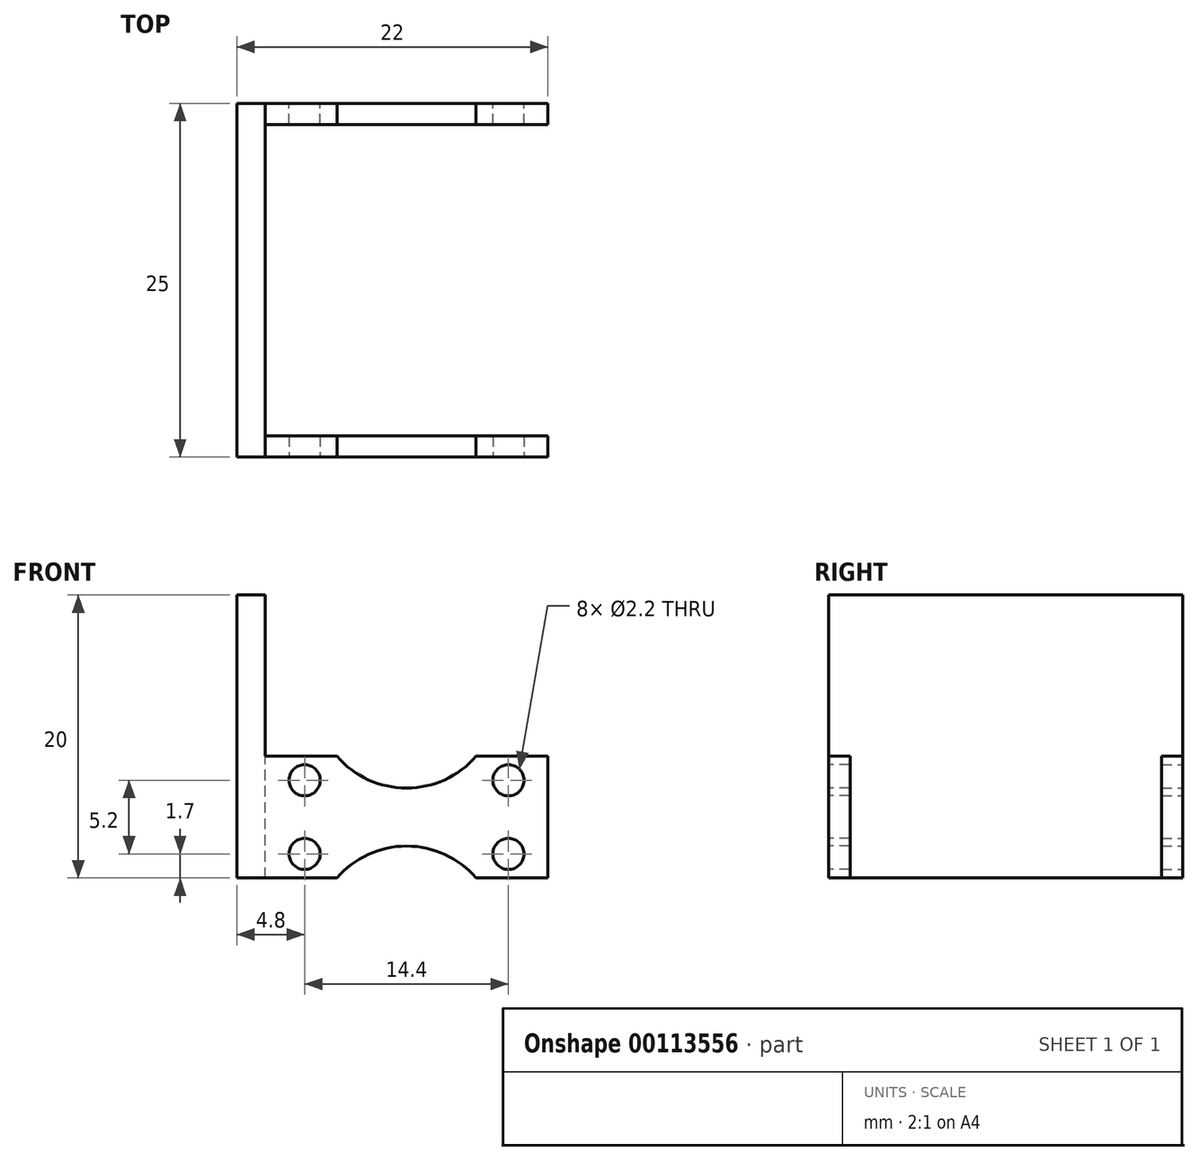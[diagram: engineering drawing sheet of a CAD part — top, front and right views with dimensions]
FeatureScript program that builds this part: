
annotation { "Feature Type Name" : "Feature", "Feature Type Description" : "" }
export const myFeature = defineFeature(function(context is Context, id is Id, definition is map)
    precondition{}
    {
        {
            var Q0;
            Q0=qCreatedBy(makeId("Front.planeOp"),FACE);
            var sketch = newSketch(context, id + "F0", { "sketchPlane" : qUnion([Q0])});
            skLineSegment(sketch, "E0.bottom", {"start": v(0, 0) * mm, "end": v(20, 0) * mm});
            skLineSegment(sketch, "E0.top", {"start": v(0, 8.6) * mm, "end": v(20, 8.6) * mm});
            skLineSegment(sketch, "E0.left", {"start": v(0, 0) * mm, "end": v(0, 8.6) * mm});
            skLineSegment(sketch, "E0.right", {"start": v(20, 0) * mm, "end": v(20, 8.6) * mm});
            skSolve(sketch);
        }
        {
            var Q0;
            Q0=qSketchRegion(id+"F0",true);
            extrude(context, id + "F1", {"entities" : qUnion([Q0]), "depth" : 1.5 * mm});
        }
        {
            var Q0;
            Q0=makeQuery(id+"F1.opExtrude","CAP_FACE",FACE,{"disambiguationData":[OSD([sQuery(id+"F0.wireOp",EDGE,"E0.bottom"),sQuery(id+"F0.wireOp",EDGE,"E0.top"),sQuery(id+"F0.wireOp",EDGE,"E0.left"),sQuery(id+"F0.wireOp",EDGE,"E0.right")])],"isStart":false});
            var sketch = newSketch(context, id + "F2", { "sketchPlane" : qUnion([Q0])});
            skLineSegment(sketch, "E1", {"start": v(0, 4.3) * mm, "end": v(20, 4.3) * mm, "construction": true});
            skLineSegment(sketch, "E2", {"start": v(10, 8.6) * mm, "end": v(10, 0) * mm, "construction": true});
            skPoint(sketch, "E3", {"position": v(10, 4.3) * mm});
            skCircle(sketch, "E4", {"center": v(2.8, 6.9) * mm, "radius": 1.1 * mm});
            skCircle(sketch, "E5.MirrorC", {"center": v(17.2, 6.9) * mm, "radius": 1.1 * mm});
            skCircle(sketch, "E6.MirrorC", {"center": v(2.8, 1.7) * mm, "radius": 1.1 * mm});
            skCircle(sketch, "E7.MirrorC", {"center": v(17.2, 1.7) * mm, "radius": 1.1 * mm});
            skLineSegment(sketch, "E8", {"start": v(0, 12.85) * mm, "end": v(19.96, 12.85) * mm, "construction": true});
            skPoint(sketch, "E9", {"position": v(10, 12.85) * mm});
            skArc(sketch, "E10", {"start": v(5.08, 8.6) * mm, "mid": v(10, 6.35) * mm, "end": v(14.92, 8.6) * mm});
            skLineSegment(sketch, "E11", {"start": v(5.08, 8.6) * mm, "end": v(14.92, 8.6) * mm});
            skArc(sketch, "E12.MirrorCS", {"start": v(5.08, 0) * mm, "mid": v(10, 2.25) * mm, "end": v(14.92, 0) * mm});
            skLineSegment(sketch, "E13.MirrorCS", {"start": v(5.08, 0) * mm, "end": v(14.92, 0) * mm});
            skSolve(sketch);
        }
        {
            var Q0;
            Q0=qSketchRegion(id+"F2",true);
            extrude(context, id + "F3", {"entities" : qUnion([Q0]), "operationType" : NewBodyOperationType.REMOVE, "endBound" : BoundingType.UP_TO_NEXT, "oppositeDirection" : true, "depth" : 25 * mm});
        }
        {
            var Q0;
            Q0=makeQuery(id+"F1.opExtrude","CAP_FACE",FACE,{"disambiguationData":[OSD([sQuery(id+"F0.wireOp",EDGE,"E0.bottom"),sQuery(id+"F0.wireOp",EDGE,"E0.top"),sQuery(id+"F0.wireOp",EDGE,"E0.left"),sQuery(id+"F0.wireOp",EDGE,"E0.right")])],"isStart":false});
            var sketch = newSketch(context, id + "F4", { "sketchPlane" : qUnion([Q0])});
            skLineSegment(sketch, "E14.bottom", {"start": v(0, 0) * mm, "end": v(-2, 0) * mm});
            skLineSegment(sketch, "E14.top", {"start": v(0, 20) * mm, "end": v(-2, 20) * mm});
            skLineSegment(sketch, "E14.left", {"start": v(0, 0) * mm, "end": v(0, 20) * mm});
            skLineSegment(sketch, "E14.right", {"start": v(-2, 0) * mm, "end": v(-2, 20) * mm});
            skSolve(sketch);
        }
        {
            var Q0;
            Q0=qSketchRegion(id+"F4",true);
            extrude(context, id + "F5", {"entities" : qUnion([Q0]), "operationType" : NewBodyOperationType.ADD, "oppositeDirection" : true, "depth" : 12.5 * mm});
        }
        {
            var Q0;
            Q0=qCreatedBy(makeId("Front.planeOp"),FACE);
            cPlane(context, id + "F6", {"entities" : qUnion([Q0]), "cplaneType" : CPlaneType.OFFSET, "offset" : 11 * mm, "oppositeDirection" : true, "width" : 150 * mm, "height" : 150 * mm});
        }
        {
            var Q0;
            Q0=makeQuery(id+"F1.opExtrude","SWEPT_BODY",BODY,{"disambiguationData":[OSD([sQuery(id+"F0.wireOp",EDGE,"E0.bottom"),sQuery(id+"F0.wireOp",EDGE,"E0.top"),sQuery(id+"F0.wireOp",EDGE,"E0.left"),sQuery(id+"F0.wireOp",EDGE,"E0.right")])]});
            var Q1;
            Q1=qCreatedBy(id+"F6.planeOp",FACE);
            mirror(context, id + "F7", {"operationType" : NewBodyOperationType.ADD, "entities" : qUnion([Q0]), "mirrorPlane" : qUnion([Q1])});
        }
    });
